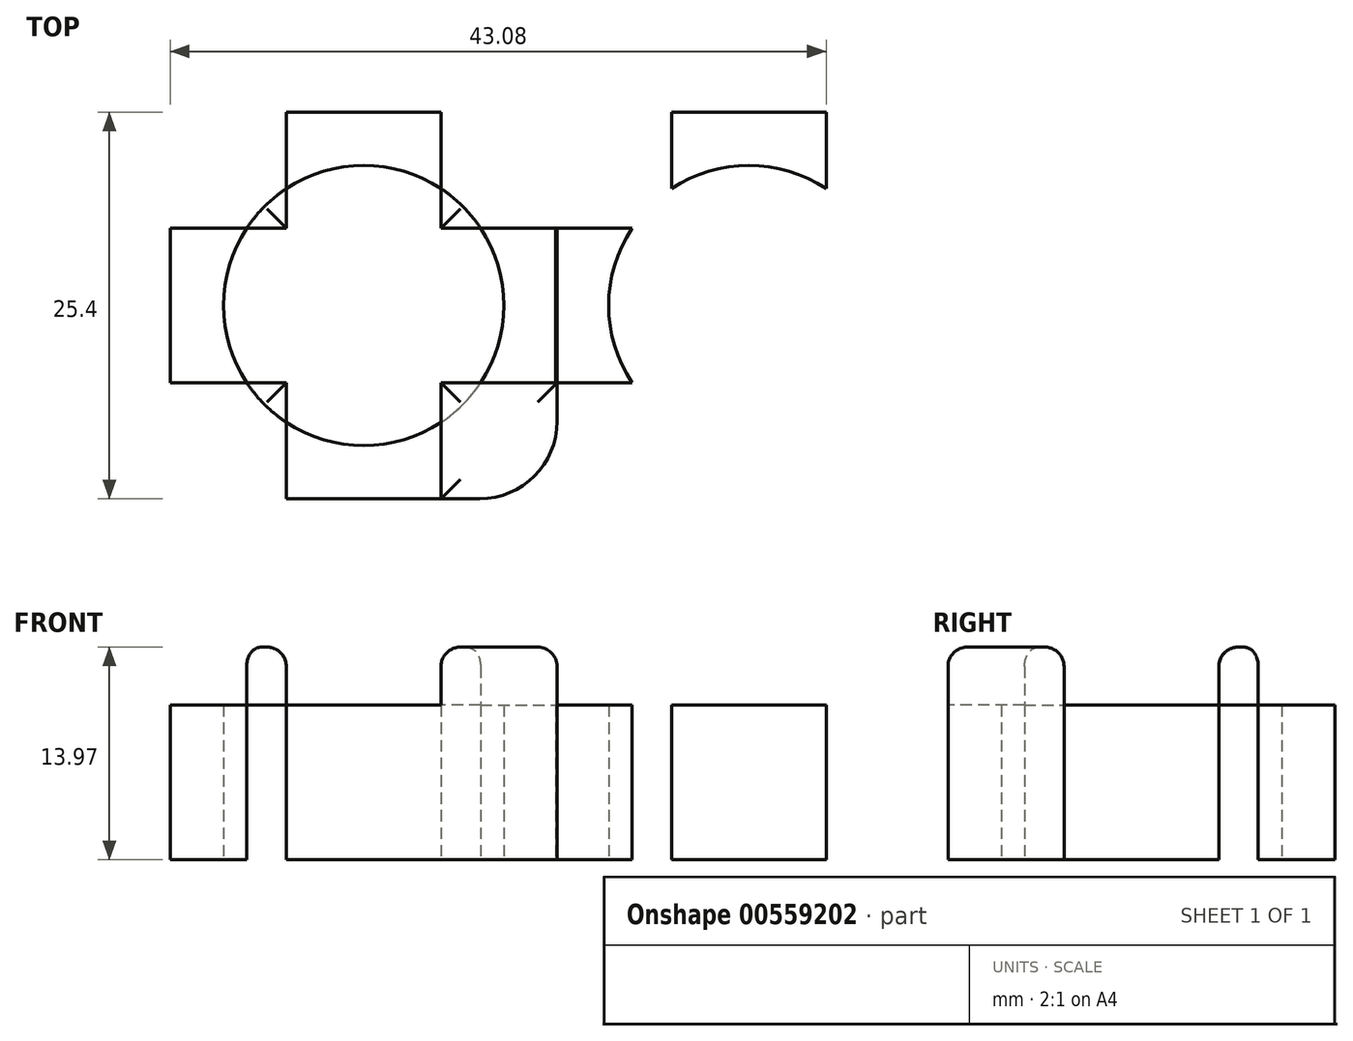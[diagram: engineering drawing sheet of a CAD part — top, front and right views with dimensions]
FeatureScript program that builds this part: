
annotation { "Feature Type Name" : "Feature", "Feature Type Description" : "" }
export const myFeature = defineFeature(function(context is Context, id is Id, definition is map)
    precondition{}
    {
        {
            var Q0;
            Q0=qCreatedBy(makeId("Top.planeOp"),FACE);
            var sketch = newSketch(context, id + "F0", { "sketchPlane" : qUnion([Q0])});
            skLineSegment(sketch, "E0.bottom", {"start": v(-11.84, 11.89) * mm, "end": v(13.56, 11.89) * mm});
            skLineSegment(sketch, "E0.top", {"start": v(-11.84, -13.51) * mm, "end": v(13.56, -13.51) * mm});
            skLineSegment(sketch, "E0.left", {"start": v(-11.84, 11.89) * mm, "end": v(-11.84, -13.51) * mm});
            skLineSegment(sketch, "E0.right", {"start": v(13.56, 11.89) * mm, "end": v(13.56, -13.51) * mm});
            skCircle(sketch, "E1", {"center": v(0.86, -0.81) * mm, "radius": 9.2 * mm});
            skPoint(sketch, "E1.centerSnap0", {"position": v(0.86, 11.89) * mm});
            skPoint(sketch, "E1.centerSnap1", {"position": v(-11.84, -0.81) * mm});
            skLineSegment(sketch, "E2.bottom", {"start": v(-11.84, 11.89) * mm, "end": v(-4.22, 11.89) * mm});
            skLineSegment(sketch, "E2.top", {"start": v(-11.84, 4.27) * mm, "end": v(-4.22, 4.27) * mm});
            skLineSegment(sketch, "E2.left", {"start": v(-11.84, 11.89) * mm, "end": v(-11.84, 4.27) * mm});
            skLineSegment(sketch, "E2.right", {"start": v(-4.22, 11.89) * mm, "end": v(-4.22, 4.27) * mm});
            skLineSegment(sketch, "E3", {"start": v(0.86, 11.89) * mm, "end": v(0.86, -16.1) * mm, "construction": true});
            skLineSegment(sketch, "E4", {"start": v(-11.84, -0.81) * mm, "end": v(13.56, -0.81) * mm, "construction": true});
            skLineSegment(sketch, "E5.MirrorCS", {"start": v(5.94, 11.89) * mm, "end": v(5.94, 4.27) * mm});
            skLineSegment(sketch, "E6.MirrorCS", {"start": v(13.56, 4.27) * mm, "end": v(5.94, 4.27) * mm});
            skLineSegment(sketch, "E7.MirrorCS", {"start": v(13.56, 11.89) * mm, "end": v(13.56, 4.27) * mm});
            skLineSegment(sketch, "E8.MirrorCS", {"start": v(13.56, 11.89) * mm, "end": v(5.94, 11.89) * mm});
            skLineSegment(sketch, "E9.MirrorCS", {"start": v(-11.84, -13.51) * mm, "end": v(-11.84, -5.9) * mm});
            skLineSegment(sketch, "E10.MirrorCS", {"start": v(-11.84, -13.51) * mm, "end": v(-4.22, -13.51) * mm});
            skLineSegment(sketch, "E11.MirrorCS", {"start": v(-4.22, -13.51) * mm, "end": v(-4.22, -5.9) * mm});
            skLineSegment(sketch, "E12.MirrorCS", {"start": v(-11.84, -5.9) * mm, "end": v(-4.22, -5.9) * mm});
            skLineSegment(sketch, "E13.MirrorCS", {"start": v(5.94, -13.51) * mm, "end": v(5.94, -5.9) * mm});
            skLineSegment(sketch, "E14.MirrorCS", {"start": v(13.56, -13.51) * mm, "end": v(13.56, 11.89) * mm});
            skLineSegment(sketch, "E15.MirrorCS", {"start": v(13.56, -5.9) * mm, "end": v(5.94, -5.9) * mm});
            skSolve(sketch);
        }
        {
            var Q0;
            {var subQ4=sQuery(id+"F0.wireOp",EDGE,"E2.bottom");Q0=makeQuery(id+"F0.imprint","IMPRINT",FACE,{"disambiguationData":[TD([[makeQuery(id+"F0.imprint","IMPRINT",EDGE,{"derivedFrom":subQ4}),-1.0]])]});}
            var Q1;
            {var subQ0=sQuery(id+"F0.wireOp",EDGE,"E2.right");var subQ1=sQuery(id+"F0.wireOp",EDGE,"E1");var subQ2=makeQuery(id+"F0.imprint","INTERSECT",VERTEX,{"derivedFrom":[subQ1,subQ0]});Q1=makeQuery(id+"F0.imprint","IMPRINT",FACE,{"disambiguationData":[TD([[makeQuery(id+"F0.imprint","IMPRINT",EDGE,{"disambiguationData":[TD([[subQ2,-1.0]])],"derivedFrom":subQ1}),1.0]])]});}
            var Q2;
            {var subQ0=sQuery(id+"F0.wireOp",EDGE,"E8.MirrorCS");Q2=makeQuery(id+"F0.imprint","IMPRINT",FACE,{"disambiguationData":[TD([[makeQuery(id+"F0.imprint","IMPRINT",EDGE,{"derivedFrom":subQ0}),1.0]])]});}
            var Q3;
            {var subQ1=sQuery(id+"F0.wireOp",EDGE,"E13.MirrorCS");var subQ5=sQuery(id+"F0.wireOp",EDGE,"E1");var subQ6=makeQuery(id+"F0.imprint","INTERSECT",VERTEX,{"derivedFrom":[subQ5,subQ1]});Q3=makeQuery(id+"F0.imprint","IMPRINT",FACE,{"disambiguationData":[TD([[makeQuery(id+"F0.imprint","IMPRINT",EDGE,{"disambiguationData":[TD([[subQ6,-1.0]])],"derivedFrom":subQ5}),-1.0]])]});}
            var Q4;
            {var subQ0=sQuery(id+"F0.wireOp",EDGE,"E11.MirrorCS");var subQ1=sQuery(id+"F0.wireOp",EDGE,"E1");var subQ2=makeQuery(id+"F0.imprint","INTERSECT",VERTEX,{"derivedFrom":[subQ1,subQ0]});Q4=makeQuery(id+"F0.imprint","IMPRINT",FACE,{"disambiguationData":[TD([[makeQuery(id+"F0.imprint","IMPRINT",EDGE,{"disambiguationData":[TD([[subQ2,-1.0]])],"derivedFrom":subQ1}),-1.0]])]});}
            var Q5;
            {var subQ1=sQuery(id+"F0.wireOp",EDGE,"E9.MirrorCS");Q5=makeQuery(id+"F0.imprint","IMPRINT",FACE,{"disambiguationData":[TD([[makeQuery(id+"F0.imprint","IMPRINT",EDGE,{"derivedFrom":subQ1}),-1.0]])]});}
            var Q6;
            {var subQ0=sQuery(id+"F0.wireOp",EDGE,"E0.left");Q6=makeQuery(id+"F0.imprint","IMPRINT",FACE,{"disambiguationData":[TD([[makeQuery(id+"F0.imprint","IMPRINT",EDGE,{"derivedFrom":subQ0}),1.0]])]});}
            var Q7;
            {var subQ0=sQuery(id+"F0.wireOp",EDGE,"E6.MirrorCS");var subQ1=sQuery(id+"F0.wireOp",EDGE,"E1");var subQ2=makeQuery(id+"F0.imprint","INTERSECT",VERTEX,{"derivedFrom":[subQ1,subQ0]});Q7=makeQuery(id+"F0.imprint","IMPRINT",FACE,{"disambiguationData":[TD([[makeQuery(id+"F0.imprint","IMPRINT",EDGE,{"disambiguationData":[TD([[subQ2,1.0]])],"derivedFrom":subQ1}),-1.0]])]});}
            var Q8;
            {var subQ0=sQuery(id+"F0.wireOp",EDGE,"E0.bottom");Q8=makeQuery(id+"F0.imprint","IMPRINT",FACE,{"disambiguationData":[TD([[makeQuery(id+"F0.imprint","IMPRINT",EDGE,{"derivedFrom":subQ0}),-1.0]])]});}
            var Q9;
            {var subQ0=sQuery(id+"F0.wireOp",EDGE,"E5.MirrorCS");var subQ1=sQuery(id+"F0.wireOp",EDGE,"E1");var subQ2=makeQuery(id+"F0.imprint","INTERSECT",VERTEX,{"derivedFrom":[subQ1,subQ0]});Q9=makeQuery(id+"F0.imprint","IMPRINT",FACE,{"disambiguationData":[TD([[makeQuery(id+"F0.imprint","IMPRINT",EDGE,{"disambiguationData":[TD([[subQ2,1.0]])],"derivedFrom":subQ1}),1.0]])]});}
            var Q10;
            {var subQ0=sQuery(id+"F0.wireOp",EDGE,"E13.MirrorCS");var subQ1=sQuery(id+"F0.wireOp",EDGE,"E1");var subQ2=makeQuery(id+"F0.imprint","INTERSECT",VERTEX,{"derivedFrom":[subQ1,subQ0]});Q10=makeQuery(id+"F0.imprint","IMPRINT",FACE,{"disambiguationData":[TD([[makeQuery(id+"F0.imprint","IMPRINT",EDGE,{"disambiguationData":[TD([[subQ2,-1.0]])],"derivedFrom":subQ1}),1.0]])]});}
            var Q11;
            {var subQ0=sQuery(id+"F0.wireOp",EDGE,"E12.MirrorCS");var subQ1=sQuery(id+"F0.wireOp",EDGE,"E1");var subQ2=makeQuery(id+"F0.imprint","INTERSECT",VERTEX,{"derivedFrom":[subQ1,subQ0]});Q11=makeQuery(id+"F0.imprint","IMPRINT",FACE,{"disambiguationData":[TD([[makeQuery(id+"F0.imprint","IMPRINT",EDGE,{"disambiguationData":[TD([[subQ2,-1.0]])],"derivedFrom":subQ1}),1.0]])]});}
            extrude(context, id + "F1", {"entities" : qUnion([Q0, Q1, Q2, Q3, Q4, Q5, Q6, Q7, Q8, Q9, Q10, Q11]), "depth" : 10.16 * mm, "offsetDistance" : 25.4 * mm});
        }
        {
            var Q0;
            {var subQ1=sQuery(id+"F0.wireOp",EDGE,"E9.MirrorCS");Q0=makeQuery(id+"F0.imprint","IMPRINT",FACE,{"disambiguationData":[TD([[makeQuery(id+"F0.imprint","IMPRINT",EDGE,{"derivedFrom":subQ1}),-1.0]])]});}
            var Q1;
            {var subQ0=sQuery(id+"F0.wireOp",EDGE,"E12.MirrorCS");var subQ1=sQuery(id+"F0.wireOp",EDGE,"E1");var subQ2=makeQuery(id+"F0.imprint","INTERSECT",VERTEX,{"derivedFrom":[subQ1,subQ0]});Q1=makeQuery(id+"F0.imprint","IMPRINT",FACE,{"disambiguationData":[TD([[makeQuery(id+"F0.imprint","IMPRINT",EDGE,{"disambiguationData":[TD([[subQ2,-1.0]])],"derivedFrom":subQ1}),1.0]])]});}
            var Q2;
            {var subQ1=sQuery(id+"F0.wireOp",EDGE,"E13.MirrorCS");var subQ5=sQuery(id+"F0.wireOp",EDGE,"E1");var subQ6=makeQuery(id+"F0.imprint","INTERSECT",VERTEX,{"derivedFrom":[subQ5,subQ1]});Q2=makeQuery(id+"F0.imprint","IMPRINT",FACE,{"disambiguationData":[TD([[makeQuery(id+"F0.imprint","IMPRINT",EDGE,{"disambiguationData":[TD([[subQ6,-1.0]])],"derivedFrom":subQ5}),-1.0]])]});}
            var Q3;
            {var subQ0=sQuery(id+"F0.wireOp",EDGE,"E13.MirrorCS");var subQ1=sQuery(id+"F0.wireOp",EDGE,"E1");var subQ2=makeQuery(id+"F0.imprint","INTERSECT",VERTEX,{"derivedFrom":[subQ1,subQ0]});Q3=makeQuery(id+"F0.imprint","IMPRINT",FACE,{"disambiguationData":[TD([[makeQuery(id+"F0.imprint","IMPRINT",EDGE,{"disambiguationData":[TD([[subQ2,-1.0]])],"derivedFrom":subQ1}),1.0]])]});}
            var Q4;
            {var subQ0=sQuery(id+"F0.wireOp",EDGE,"E8.MirrorCS");Q4=makeQuery(id+"F0.imprint","IMPRINT",FACE,{"disambiguationData":[TD([[makeQuery(id+"F0.imprint","IMPRINT",EDGE,{"derivedFrom":subQ0}),1.0]])]});}
            var Q5;
            {var subQ0=sQuery(id+"F0.wireOp",EDGE,"E5.MirrorCS");var subQ1=sQuery(id+"F0.wireOp",EDGE,"E1");var subQ2=makeQuery(id+"F0.imprint","INTERSECT",VERTEX,{"derivedFrom":[subQ1,subQ0]});Q5=makeQuery(id+"F0.imprint","IMPRINT",FACE,{"disambiguationData":[TD([[makeQuery(id+"F0.imprint","IMPRINT",EDGE,{"disambiguationData":[TD([[subQ2,1.0]])],"derivedFrom":subQ1}),1.0]])]});}
            var Q6;
            {var subQ4=sQuery(id+"F0.wireOp",EDGE,"E2.bottom");Q6=makeQuery(id+"F0.imprint","IMPRINT",FACE,{"disambiguationData":[TD([[makeQuery(id+"F0.imprint","IMPRINT",EDGE,{"derivedFrom":subQ4}),-1.0]])]});}
            var Q7;
            {var subQ0=sQuery(id+"F0.wireOp",EDGE,"E2.right");var subQ1=sQuery(id+"F0.wireOp",EDGE,"E1");var subQ2=makeQuery(id+"F0.imprint","INTERSECT",VERTEX,{"derivedFrom":[subQ1,subQ0]});Q7=makeQuery(id+"F0.imprint","IMPRINT",FACE,{"disambiguationData":[TD([[makeQuery(id+"F0.imprint","IMPRINT",EDGE,{"disambiguationData":[TD([[subQ2,-1.0]])],"derivedFrom":subQ1}),1.0]])]});}
            extrude(context, id + "F2", {"entities" : qUnion([Q0, Q1, Q2, Q3, Q4, Q5, Q6, Q7]), "operationType" : NewBodyOperationType.ADD, "depth" : 13.97 * mm, "offsetDistance" : 25.4 * mm});
        }
        {
            var Q0;
            {var subQ0=sQuery(id+"F0.wireOp",EDGE,"E2.right");var subQ1=sQuery(id+"F0.wireOp",EDGE,"E1");var subQ2=makeQuery(id+"F0.imprint","INTERSECT",VERTEX,{"derivedFrom":[subQ1,subQ0]});Q0=makeQuery(id+"F0.imprint","IMPRINT",FACE,{"disambiguationData":[TD([[makeQuery(id+"F0.imprint","IMPRINT",EDGE,{"disambiguationData":[TD([[subQ2,-1.0]])],"derivedFrom":subQ1}),1.0]])]});}
            var Q1;
            {var subQ0=sQuery(id+"F0.wireOp",EDGE,"E12.MirrorCS");var subQ1=sQuery(id+"F0.wireOp",EDGE,"E1");var subQ2=makeQuery(id+"F0.imprint","INTERSECT",VERTEX,{"derivedFrom":[subQ1,subQ0]});Q1=makeQuery(id+"F0.imprint","IMPRINT",FACE,{"disambiguationData":[TD([[makeQuery(id+"F0.imprint","IMPRINT",EDGE,{"disambiguationData":[TD([[subQ2,-1.0]])],"derivedFrom":subQ1}),1.0]])]});}
            var Q2;
            {var subQ0=sQuery(id+"F0.wireOp",EDGE,"E13.MirrorCS");var subQ1=sQuery(id+"F0.wireOp",EDGE,"E1");var subQ2=makeQuery(id+"F0.imprint","INTERSECT",VERTEX,{"derivedFrom":[subQ1,subQ0]});Q2=makeQuery(id+"F0.imprint","IMPRINT",FACE,{"disambiguationData":[TD([[makeQuery(id+"F0.imprint","IMPRINT",EDGE,{"disambiguationData":[TD([[subQ2,-1.0]])],"derivedFrom":subQ1}),1.0]])]});}
            var Q3;
            {var subQ0=sQuery(id+"F0.wireOp",EDGE,"E5.MirrorCS");var subQ1=sQuery(id+"F0.wireOp",EDGE,"E1");var subQ2=makeQuery(id+"F0.imprint","INTERSECT",VERTEX,{"derivedFrom":[subQ1,subQ0]});Q3=makeQuery(id+"F0.imprint","IMPRINT",FACE,{"disambiguationData":[TD([[makeQuery(id+"F0.imprint","IMPRINT",EDGE,{"disambiguationData":[TD([[subQ2,1.0]])],"derivedFrom":subQ1}),1.0]])]});}
            extrude(context, id + "F3", {"entities" : qUnion([Q0, Q1, Q2, Q3]), "operationType" : NewBodyOperationType.REMOVE, "depth" : 10.16 * mm, "offsetDistance" : 25.4 * mm});
        }
        {
            var Q0;
            Q0=makeQuery(id+"F1.opExtrude","SWEPT_BODY",BODY,{"disambiguationData":[OSD([sQuery(id+"F0.wireOp",EDGE,"E0.bottom"),sQuery(id+"F0.wireOp",EDGE,"E0.left"),sQuery(id+"F0.wireOp",EDGE,"E1"),sQuery(id+"F0.wireOp",EDGE,"E2.bottom"),sQuery(id+"F0.wireOp",EDGE,"E2.top"),sQuery(id+"F0.wireOp",EDGE,"E2.left"),sQuery(id+"F0.wireOp",EDGE,"E2.right"),sQuery(id+"F0.wireOp",EDGE,"E5.MirrorCS"),sQuery(id+"F0.wireOp",EDGE,"E6.MirrorCS"),sQuery(id+"F0.wireOp",EDGE,"E8.MirrorCS"),sQuery(id+"F0.wireOp",EDGE,"E9.MirrorCS"),sQuery(id+"F0.wireOp",EDGE,"E11.MirrorCS"),sQuery(id+"F0.wireOp",EDGE,"E12.MirrorCS"),sQuery(id+"F0.wireOp",EDGE,"E13.MirrorCS"),sQuery(id+"F0.wireOp",EDGE,"E0.top"),sQuery(id+"F0.wireOp",EDGE,"E14.MirrorCS"),sQuery(id+"F0.wireOp",EDGE,"E15.MirrorCS")])]});
            transform(context, id + "F4", {"entities" : qUnion([Q0]), "transformType" : TransformType.TRANSLATION_3D, "dx" : 25.65 * mm, "dy" : 0 * mm, "dz" : 0 * mm, "makeCopy" : true});
        }
        {
            var Q0;
            Q0=makeQuery(id+"F4.opPattern","COPY",BODY,{"derivedFrom":makeQuery(id+"F1.opExtrude","SWEPT_BODY",BODY,{"disambiguationData":[OSD([sQuery(id+"F0.wireOp",EDGE,"E0.bottom"),sQuery(id+"F0.wireOp",EDGE,"E0.left"),sQuery(id+"F0.wireOp",EDGE,"E1"),sQuery(id+"F0.wireOp",EDGE,"E2.bottom"),sQuery(id+"F0.wireOp",EDGE,"E2.top"),sQuery(id+"F0.wireOp",EDGE,"E2.left"),sQuery(id+"F0.wireOp",EDGE,"E2.right"),sQuery(id+"F0.wireOp",EDGE,"E5.MirrorCS"),sQuery(id+"F0.wireOp",EDGE,"E6.MirrorCS"),sQuery(id+"F0.wireOp",EDGE,"E8.MirrorCS"),sQuery(id+"F0.wireOp",EDGE,"E9.MirrorCS"),sQuery(id+"F0.wireOp",EDGE,"E11.MirrorCS"),sQuery(id+"F0.wireOp",EDGE,"E12.MirrorCS"),sQuery(id+"F0.wireOp",EDGE,"E13.MirrorCS"),sQuery(id+"F0.wireOp",EDGE,"E0.top"),sQuery(id+"F0.wireOp",EDGE,"E14.MirrorCS"),sQuery(id+"F0.wireOp",EDGE,"E15.MirrorCS")])]}),"instanceName":"1"});
            deleteBodies(context, id + "F5", {"entities" : qUnion([Q0])});
        }
        {
            var Q0;
            Q0=makeQuery(id+"F1.opExtrude","SWEPT_BODY",BODY,{"disambiguationData":[OSD([sQuery(id+"F0.wireOp",EDGE,"E0.bottom"),sQuery(id+"F0.wireOp",EDGE,"E0.left"),sQuery(id+"F0.wireOp",EDGE,"E1"),sQuery(id+"F0.wireOp",EDGE,"E2.bottom"),sQuery(id+"F0.wireOp",EDGE,"E2.top"),sQuery(id+"F0.wireOp",EDGE,"E2.left"),sQuery(id+"F0.wireOp",EDGE,"E2.right"),sQuery(id+"F0.wireOp",EDGE,"E5.MirrorCS"),sQuery(id+"F0.wireOp",EDGE,"E6.MirrorCS"),sQuery(id+"F0.wireOp",EDGE,"E8.MirrorCS"),sQuery(id+"F0.wireOp",EDGE,"E9.MirrorCS"),sQuery(id+"F0.wireOp",EDGE,"E11.MirrorCS"),sQuery(id+"F0.wireOp",EDGE,"E12.MirrorCS"),sQuery(id+"F0.wireOp",EDGE,"E13.MirrorCS"),sQuery(id+"F0.wireOp",EDGE,"E0.top"),sQuery(id+"F0.wireOp",EDGE,"E14.MirrorCS"),sQuery(id+"F0.wireOp",EDGE,"E15.MirrorCS")])]});
            transform(context, id + "F6", {"entities" : qUnion([Q0]), "transformType" : TransformType.TRANSLATION_3D, "dx" : 25.3 * mm, "dy" : 0 * mm, "dz" : 0 * mm, "makeCopy" : true});
        }
        {
            var Q0;
            Q0=makeQuery(id+"F1.opExtrude","SWEPT_BODY",BODY,{"disambiguationData":[OSD([sQuery(id+"F0.wireOp",EDGE,"E0.bottom"),sQuery(id+"F0.wireOp",EDGE,"E0.left"),sQuery(id+"F0.wireOp",EDGE,"E1"),sQuery(id+"F0.wireOp",EDGE,"E2.bottom"),sQuery(id+"F0.wireOp",EDGE,"E2.top"),sQuery(id+"F0.wireOp",EDGE,"E2.left"),sQuery(id+"F0.wireOp",EDGE,"E2.right"),sQuery(id+"F0.wireOp",EDGE,"E5.MirrorCS"),sQuery(id+"F0.wireOp",EDGE,"E6.MirrorCS"),sQuery(id+"F0.wireOp",EDGE,"E8.MirrorCS"),sQuery(id+"F0.wireOp",EDGE,"E9.MirrorCS"),sQuery(id+"F0.wireOp",EDGE,"E11.MirrorCS"),sQuery(id+"F0.wireOp",EDGE,"E12.MirrorCS"),sQuery(id+"F0.wireOp",EDGE,"E13.MirrorCS"),sQuery(id+"F0.wireOp",EDGE,"E0.top"),sQuery(id+"F0.wireOp",EDGE,"E14.MirrorCS"),sQuery(id+"F0.wireOp",EDGE,"E15.MirrorCS")])]});
            var Q1;
            Q1=makeQuery(id+"F6.opPattern","COPY",BODY,{"derivedFrom":makeQuery(id+"F1.opExtrude","SWEPT_BODY",BODY,{"disambiguationData":[OSD([sQuery(id+"F0.wireOp",EDGE,"E0.bottom"),sQuery(id+"F0.wireOp",EDGE,"E0.left"),sQuery(id+"F0.wireOp",EDGE,"E1"),sQuery(id+"F0.wireOp",EDGE,"E2.bottom"),sQuery(id+"F0.wireOp",EDGE,"E2.top"),sQuery(id+"F0.wireOp",EDGE,"E2.left"),sQuery(id+"F0.wireOp",EDGE,"E2.right"),sQuery(id+"F0.wireOp",EDGE,"E5.MirrorCS"),sQuery(id+"F0.wireOp",EDGE,"E6.MirrorCS"),sQuery(id+"F0.wireOp",EDGE,"E8.MirrorCS"),sQuery(id+"F0.wireOp",EDGE,"E9.MirrorCS"),sQuery(id+"F0.wireOp",EDGE,"E11.MirrorCS"),sQuery(id+"F0.wireOp",EDGE,"E12.MirrorCS"),sQuery(id+"F0.wireOp",EDGE,"E13.MirrorCS"),sQuery(id+"F0.wireOp",EDGE,"E0.top"),sQuery(id+"F0.wireOp",EDGE,"E14.MirrorCS"),sQuery(id+"F0.wireOp",EDGE,"E15.MirrorCS")])]}),"instanceName":"1"});
            booleanBodies(context, id + "F7", {"operationType" : BooleanOperationType.UNION, "tools" : qUnion([Q0, Q1])});
        }
        {
            var Q0;
            {var subQ0=sQuery(id+"F0.wireOp",EDGE,"E2.left");var subQ1=sQuery(id+"F0.wireOp",EDGE,"E2.bottom");Q0=makeQuery(id+"F2.boolean.opBoolean","MERGE",EDGE,{"derivedFrom":[makeQuery(id+"F1.opExtrude","SWEPT_EDGE",EDGE,{"disambiguationData":[OSD([subQ1,subQ0])]}),makeQuery(id+"F2.opExtrude","SWEPT_EDGE",EDGE,{"disambiguationData":[OSD([subQ1,subQ0])]})]});}
            var Q1;
            {var subQ0=sQuery(id+"F0.wireOp",EDGE,"E14.MirrorCS");var subQ1=sQuery(id+"F0.wireOp",EDGE,"E8.MirrorCS");Q1=makeQuery(id+"F6.opPattern","COPY",EDGE,{"derivedFrom":makeQuery(id+"F2.boolean.opBoolean","MERGE",EDGE,{"derivedFrom":[makeQuery(id+"F1.opExtrude","SWEPT_EDGE",EDGE,{"disambiguationData":[OSD([subQ1,subQ0])]}),makeQuery(id+"F2.opExtrude","SWEPT_EDGE",EDGE,{"disambiguationData":[OSD([subQ1,subQ0])]})]}),"instanceName":"1"});}
            var Q2;
            {var subQ0=sQuery(id+"F0.wireOp",EDGE,"E14.MirrorCS");var subQ1=sQuery(id+"F0.wireOp",EDGE,"E0.top");Q2=makeQuery(id+"F6.opPattern","COPY",EDGE,{"derivedFrom":makeQuery(id+"F2.boolean.opBoolean","MERGE",EDGE,{"derivedFrom":[makeQuery(id+"F1.opExtrude","SWEPT_EDGE",EDGE,{"disambiguationData":[OSD([subQ1,subQ0])]}),makeQuery(id+"F2.opExtrude","SWEPT_EDGE",EDGE,{"disambiguationData":[OSD([subQ1,subQ0])]})]}),"instanceName":"1"});}
            var Q3;
            {var subQ0=sQuery(id+"F0.wireOp",EDGE,"E0.top");var subQ1=sQuery(id+"F0.wireOp",EDGE,"E9.MirrorCS");Q3=makeQuery(id+"F2.boolean.opBoolean","MERGE",EDGE,{"derivedFrom":[makeQuery(id+"F1.opExtrude","SWEPT_EDGE",EDGE,{"disambiguationData":[OSD([subQ1,subQ0])]}),makeQuery(id+"F2.opExtrude","SWEPT_EDGE",EDGE,{"disambiguationData":[OSD([subQ1,subQ0])]})]});}
            fillet(context, id + "F8", {"entities" : qUnion([Q0, Q1, Q2, Q3]), "radius" : 5.08 * mm, "tangentPropagation" : true, "allowEdgeOverflow" : false});
        }
        {
            var Q0;
            {var subQ0=sQuery(id+"F0.wireOp",EDGE,"E2.left");var subQ1=sQuery(id+"F0.wireOp",EDGE,"E2.bottom");Q0=makeQuery(id+"F8.opFillet","BLEND_EDGE",EDGE,{"blendedFrom":[makeQuery(id+"F2.boolean.opBoolean","MERGE",EDGE,{"derivedFrom":[makeQuery(id+"F1.opExtrude","SWEPT_EDGE",EDGE,{"disambiguationData":[OSD([subQ1,subQ0])]}),makeQuery(id+"F2.opExtrude","SWEPT_EDGE",EDGE,{"disambiguationData":[OSD([subQ1,subQ0])]})]}),makeQuery(id+"F2.opExtrude","CAP_FACE",FACE,{"disambiguationData":[OSD([subQ1,sQuery(id+"F0.wireOp",EDGE,"E2.top"),subQ0,sQuery(id+"F0.wireOp",EDGE,"E2.right")])],"isStart":false})],"blendedInto":[makeQuery(id+"F2.opExtrude","CAP_FACE",FACE,{"disambiguationData":[OSD([subQ1,sQuery(id+"F0.wireOp",EDGE,"E2.top"),subQ0,sQuery(id+"F0.wireOp",EDGE,"E2.right")])],"isStart":false})]});}
            var Q1;
            Q1=makeQuery(id+"F2.opExtrude","CAP_EDGE",EDGE,{"disambiguationData":[OSD([sQuery(id+"F0.wireOp",EDGE,"E2.right")])],"isStart":false});
            var Q2;
            Q2=makeQuery(id+"F2.opExtrude","CAP_EDGE",EDGE,{"disambiguationData":[OSD([sQuery(id+"F0.wireOp",EDGE,"E2.top")])],"isStart":false});
            var Q3;
            Q3=makeQuery(id+"F2.opExtrude","CAP_EDGE",EDGE,{"disambiguationData":[OSD([sQuery(id+"F0.wireOp",EDGE,"E12.MirrorCS")])],"isStart":false});
            var Q4;
            Q4=makeQuery(id+"F2.opExtrude","CAP_EDGE",EDGE,{"disambiguationData":[OSD([sQuery(id+"F0.wireOp",EDGE,"E11.MirrorCS")])],"isStart":false});
            var Q5;
            {var subQ0=sQuery(id+"F0.wireOp",EDGE,"E0.top");var subQ1=sQuery(id+"F0.wireOp",EDGE,"E9.MirrorCS");Q5=makeQuery(id+"F8.opFillet","BLEND_EDGE",EDGE,{"blendedFrom":[makeQuery(id+"F2.boolean.opBoolean","MERGE",EDGE,{"derivedFrom":[makeQuery(id+"F1.opExtrude","SWEPT_EDGE",EDGE,{"disambiguationData":[OSD([subQ1,subQ0])]}),makeQuery(id+"F2.opExtrude","SWEPT_EDGE",EDGE,{"disambiguationData":[OSD([subQ1,subQ0])]})]}),makeQuery(id+"F2.opExtrude","CAP_FACE",FACE,{"disambiguationData":[OSD([subQ1,sQuery(id+"F0.wireOp",EDGE,"E11.MirrorCS"),sQuery(id+"F0.wireOp",EDGE,"E12.MirrorCS"),subQ0])],"isStart":false})],"blendedInto":[makeQuery(id+"F2.opExtrude","CAP_FACE",FACE,{"disambiguationData":[OSD([subQ1,sQuery(id+"F0.wireOp",EDGE,"E11.MirrorCS"),sQuery(id+"F0.wireOp",EDGE,"E12.MirrorCS"),subQ0])],"isStart":false})]});}
            var Q6;
            Q6=makeQuery(id+"F2.opExtrude","CAP_EDGE",EDGE,{"disambiguationData":[OSD([sQuery(id+"F0.wireOp",EDGE,"E13.MirrorCS")])],"isStart":false});
            var Q7;
            Q7=makeQuery(id+"F7.opBoolean","MERGE",EDGE,{"derivedFrom":[makeQuery(id+"F2.opExtrude","CAP_EDGE",EDGE,{"disambiguationData":[OSD([sQuery(id+"F0.wireOp",EDGE,"E15.MirrorCS")])],"isStart":false}),makeQuery(id+"F6.opPattern","COPY",EDGE,{"derivedFrom":makeQuery(id+"F2.opExtrude","CAP_EDGE",EDGE,{"disambiguationData":[OSD([sQuery(id+"F0.wireOp",EDGE,"E12.MirrorCS")])],"isStart":false}),"instanceName":"1"})]});
            var Q8;
            {var subQ0=sQuery(id+"F0.wireOp",EDGE,"E0.top");Q8=makeQuery(id+"F7.opBoolean","MERGE",EDGE,{"derivedFrom":[makeQuery(id+"F2.opExtrude","CAP_EDGE",EDGE,{"disambiguationData":[OSD([subQ0]),TDD([makeQuery(id+"F0.imprint","IMPRINT",EDGE,{"disambiguationData":[TD([[makeQuery(id+"F0.imprint","INTERSECT",VERTEX,{"derivedFrom":[sQuery(id+"F0.wireOp",EDGE,"E13.MirrorCS"),subQ0]}),-1.0]])],"derivedFrom":subQ0})])],"isStart":false}),makeQuery(id+"F6.opPattern","COPY",EDGE,{"derivedFrom":makeQuery(id+"F2.opExtrude","CAP_EDGE",EDGE,{"disambiguationData":[OSD([subQ0]),TDD([makeQuery(id+"F0.imprint","IMPRINT",EDGE,{"disambiguationData":[TD([[makeQuery(id+"F0.imprint","INTERSECT",VERTEX,{"derivedFrom":[sQuery(id+"F0.wireOp",EDGE,"E9.MirrorCS"),subQ0]}),-1.0]])],"derivedFrom":subQ0})])],"isStart":false}),"instanceName":"1"})]});}
            var Q9;
            Q9=makeQuery(id+"F6.opPattern","COPY",EDGE,{"derivedFrom":makeQuery(id+"F2.opExtrude","CAP_EDGE",EDGE,{"disambiguationData":[OSD([sQuery(id+"F0.wireOp",EDGE,"E11.MirrorCS")])],"isStart":false}),"instanceName":"1"});
            var Q10;
            Q10=makeQuery(id+"F7.opBoolean","MERGE",EDGE,{"derivedFrom":[makeQuery(id+"F2.opExtrude","CAP_EDGE",EDGE,{"disambiguationData":[OSD([sQuery(id+"F0.wireOp",EDGE,"E8.MirrorCS")])],"isStart":false}),makeQuery(id+"F6.opPattern","COPY",EDGE,{"derivedFrom":makeQuery(id+"F2.opExtrude","CAP_EDGE",EDGE,{"disambiguationData":[OSD([sQuery(id+"F0.wireOp",EDGE,"E2.bottom")])],"isStart":false}),"instanceName":"1"})]});
            var Q11;
            Q11=makeQuery(id+"F2.opExtrude","CAP_EDGE",EDGE,{"disambiguationData":[OSD([sQuery(id+"F0.wireOp",EDGE,"E5.MirrorCS")])],"isStart":false});
            var Q12;
            Q12=makeQuery(id+"F6.opPattern","COPY",EDGE,{"derivedFrom":makeQuery(id+"F2.opExtrude","CAP_EDGE",EDGE,{"disambiguationData":[OSD([sQuery(id+"F0.wireOp",EDGE,"E2.right")])],"isStart":false}),"instanceName":"1"});
            var Q13;
            Q13=makeQuery(id+"F7.opBoolean","MERGE",EDGE,{"derivedFrom":[makeQuery(id+"F2.opExtrude","CAP_EDGE",EDGE,{"disambiguationData":[OSD([sQuery(id+"F0.wireOp",EDGE,"E6.MirrorCS")])],"isStart":false}),makeQuery(id+"F6.opPattern","COPY",EDGE,{"derivedFrom":makeQuery(id+"F2.opExtrude","CAP_EDGE",EDGE,{"disambiguationData":[OSD([sQuery(id+"F0.wireOp",EDGE,"E2.top")])],"isStart":false}),"instanceName":"1"})]});
            var Q14;
            Q14=makeQuery(id+"F6.opPattern","COPY",EDGE,{"derivedFrom":makeQuery(id+"F2.opExtrude","CAP_EDGE",EDGE,{"disambiguationData":[OSD([sQuery(id+"F0.wireOp",EDGE,"E5.MirrorCS")])],"isStart":false}),"instanceName":"1"});
            var Q15;
            Q15=makeQuery(id+"F6.opPattern","COPY",EDGE,{"derivedFrom":makeQuery(id+"F2.opExtrude","CAP_EDGE",EDGE,{"disambiguationData":[OSD([sQuery(id+"F0.wireOp",EDGE,"E6.MirrorCS")])],"isStart":false}),"instanceName":"1"});
            var Q16;
            Q16=makeQuery(id+"F6.opPattern","COPY",EDGE,{"derivedFrom":makeQuery(id+"F2.opExtrude","CAP_EDGE",EDGE,{"disambiguationData":[OSD([sQuery(id+"F0.wireOp",EDGE,"E15.MirrorCS")])],"isStart":false}),"instanceName":"1"});
            var Q17;
            Q17=makeQuery(id+"F6.opPattern","COPY",EDGE,{"derivedFrom":makeQuery(id+"F2.opExtrude","CAP_EDGE",EDGE,{"disambiguationData":[OSD([sQuery(id+"F0.wireOp",EDGE,"E13.MirrorCS")])],"isStart":false}),"instanceName":"1"});
            var Q18;
            {var subQ0=sQuery(id+"F0.wireOp",EDGE,"E14.MirrorCS");var subQ1=sQuery(id+"F0.wireOp",EDGE,"E8.MirrorCS");Q18=makeQuery(id+"F8.opFillet","BLEND_EDGE",EDGE,{"blendedFrom":[makeQuery(id+"F6.opPattern","COPY",EDGE,{"derivedFrom":makeQuery(id+"F2.boolean.opBoolean","MERGE",EDGE,{"derivedFrom":[makeQuery(id+"F1.opExtrude","SWEPT_EDGE",EDGE,{"disambiguationData":[OSD([subQ1,subQ0])]}),makeQuery(id+"F2.opExtrude","SWEPT_EDGE",EDGE,{"disambiguationData":[OSD([subQ1,subQ0])]})]}),"instanceName":"1"}),makeQuery(id+"F6.opPattern","COPY",FACE,{"derivedFrom":makeQuery(id+"F2.opExtrude","CAP_FACE",FACE,{"disambiguationData":[OSD([sQuery(id+"F0.wireOp",EDGE,"E5.MirrorCS"),sQuery(id+"F0.wireOp",EDGE,"E6.MirrorCS"),subQ1,subQ0])],"isStart":false}),"instanceName":"1"})],"blendedInto":[makeQuery(id+"F6.opPattern","COPY",FACE,{"derivedFrom":makeQuery(id+"F2.opExtrude","CAP_FACE",FACE,{"disambiguationData":[OSD([sQuery(id+"F0.wireOp",EDGE,"E5.MirrorCS"),sQuery(id+"F0.wireOp",EDGE,"E6.MirrorCS"),subQ1,subQ0])],"isStart":false}),"instanceName":"1"})]});}
            var Q19;
            {var subQ0=sQuery(id+"F0.wireOp",EDGE,"E14.MirrorCS");var subQ1=sQuery(id+"F0.wireOp",EDGE,"E0.top");Q19=makeQuery(id+"F8.opFillet","BLEND_EDGE",EDGE,{"blendedFrom":[makeQuery(id+"F6.opPattern","COPY",EDGE,{"derivedFrom":makeQuery(id+"F2.boolean.opBoolean","MERGE",EDGE,{"derivedFrom":[makeQuery(id+"F1.opExtrude","SWEPT_EDGE",EDGE,{"disambiguationData":[OSD([subQ1,subQ0])]}),makeQuery(id+"F2.opExtrude","SWEPT_EDGE",EDGE,{"disambiguationData":[OSD([subQ1,subQ0])]})]}),"instanceName":"1"}),makeQuery(id+"F6.opPattern","COPY",FACE,{"derivedFrom":makeQuery(id+"F2.opExtrude","CAP_FACE",FACE,{"disambiguationData":[OSD([sQuery(id+"F0.wireOp",EDGE,"E13.MirrorCS"),subQ1,subQ0,sQuery(id+"F0.wireOp",EDGE,"E15.MirrorCS")])],"isStart":false}),"instanceName":"1"})],"blendedInto":[makeQuery(id+"F6.opPattern","COPY",FACE,{"derivedFrom":makeQuery(id+"F2.opExtrude","CAP_FACE",FACE,{"disambiguationData":[OSD([sQuery(id+"F0.wireOp",EDGE,"E13.MirrorCS"),subQ1,subQ0,sQuery(id+"F0.wireOp",EDGE,"E15.MirrorCS")])],"isStart":false}),"instanceName":"1"})]});}
            fillet(context, id + "F9", {"entities" : qUnion([Q0, Q1, Q2, Q3, Q4, Q5, Q6, Q7, Q8, Q9, Q10, Q11, Q12, Q13, Q14, Q15, Q16, Q17, Q18, Q19]), "radius" : 1.27 * mm, "tangentPropagation" : true, "allowEdgeOverflow" : false});
        }
        {
            var Q0;
            {var subQ0=sQuery(id+"F0.wireOp",EDGE,"E0.top");var subQ1=makeQuery(id+"F2.boolean.opBoolean","MERGE",FACE,{"derivedFrom":[makeQuery(id+"F1.opExtrude","SWEPT_FACE",FACE,{"disambiguationData":[OSD([subQ0])]}),makeQuery(id+"F2.opExtrude","SWEPT_FACE",FACE,{"disambiguationData":[OSD([subQ0]),TDD([makeQuery(id+"F0.imprint","IMPRINT",EDGE,{"disambiguationData":[TD([[makeQuery(id+"F0.imprint","INTERSECT",VERTEX,{"derivedFrom":[sQuery(id+"F0.wireOp",EDGE,"E9.MirrorCS"),subQ0]}),-1.0]])],"derivedFrom":subQ0})])]}),makeQuery(id+"F2.opExtrude","SWEPT_FACE",FACE,{"disambiguationData":[OSD([subQ0]),TDD([makeQuery(id+"F0.imprint","IMPRINT",EDGE,{"disambiguationData":[TD([[makeQuery(id+"F0.imprint","INTERSECT",VERTEX,{"derivedFrom":[sQuery(id+"F0.wireOp",EDGE,"E13.MirrorCS"),subQ0]}),-1.0]])],"derivedFrom":subQ0})])]})]});Q0=makeQuery(id+"F7.opBoolean","MERGE",FACE,{"derivedFrom":[subQ1,makeQuery(id+"F6.opPattern","COPY",FACE,{"derivedFrom":subQ1,"instanceName":"1"})]});}
            var sketch = newSketch(context, id + "F10", { "sketchPlane" : qUnion([Q0])});
            skPoint(sketch, "E16", {"position": v(13.51, 5.71) * mm});
            skPoint(sketch, "E16.positionSnap0", {"position": v(13.51, 0) * mm});
            skSolve(sketch);
        }
        {
            var Q0;
            Q0=sQuery(id+"F10.wireOp",VERTEX,"E16");
            var Q1;
            Q1=makeQuery(id+"F1.opExtrude","SWEPT_BODY",BODY,{"disambiguationData":[OSD([sQuery(id+"F0.wireOp",EDGE,"E0.bottom"),sQuery(id+"F0.wireOp",EDGE,"E0.left"),sQuery(id+"F0.wireOp",EDGE,"E1"),sQuery(id+"F0.wireOp",EDGE,"E2.bottom"),sQuery(id+"F0.wireOp",EDGE,"E2.top"),sQuery(id+"F0.wireOp",EDGE,"E2.left"),sQuery(id+"F0.wireOp",EDGE,"E2.right"),sQuery(id+"F0.wireOp",EDGE,"E5.MirrorCS"),sQuery(id+"F0.wireOp",EDGE,"E6.MirrorCS"),sQuery(id+"F0.wireOp",EDGE,"E8.MirrorCS"),sQuery(id+"F0.wireOp",EDGE,"E9.MirrorCS"),sQuery(id+"F0.wireOp",EDGE,"E11.MirrorCS"),sQuery(id+"F0.wireOp",EDGE,"E12.MirrorCS"),sQuery(id+"F0.wireOp",EDGE,"E13.MirrorCS"),sQuery(id+"F0.wireOp",EDGE,"E0.top"),sQuery(id+"F0.wireOp",EDGE,"E14.MirrorCS"),sQuery(id+"F0.wireOp",EDGE,"E15.MirrorCS")])]});
            hole(context, id + "F11", {"style" : HoleStyle.C_SINK, "endStyle" : HoleEndStyle.THROUGH, "holeDiameter" : 4.44 * mm, "cSinkDiameter" : 8.9 * mm, "cSinkAngle" : 90 * degree, "isTappedThrough" : true, "tappedDepth" : 12.7 * mm, "tapClearance" : 3, "locations" : qUnion([Q0]), "scope" : qUnion([Q1])});
        }
    });
